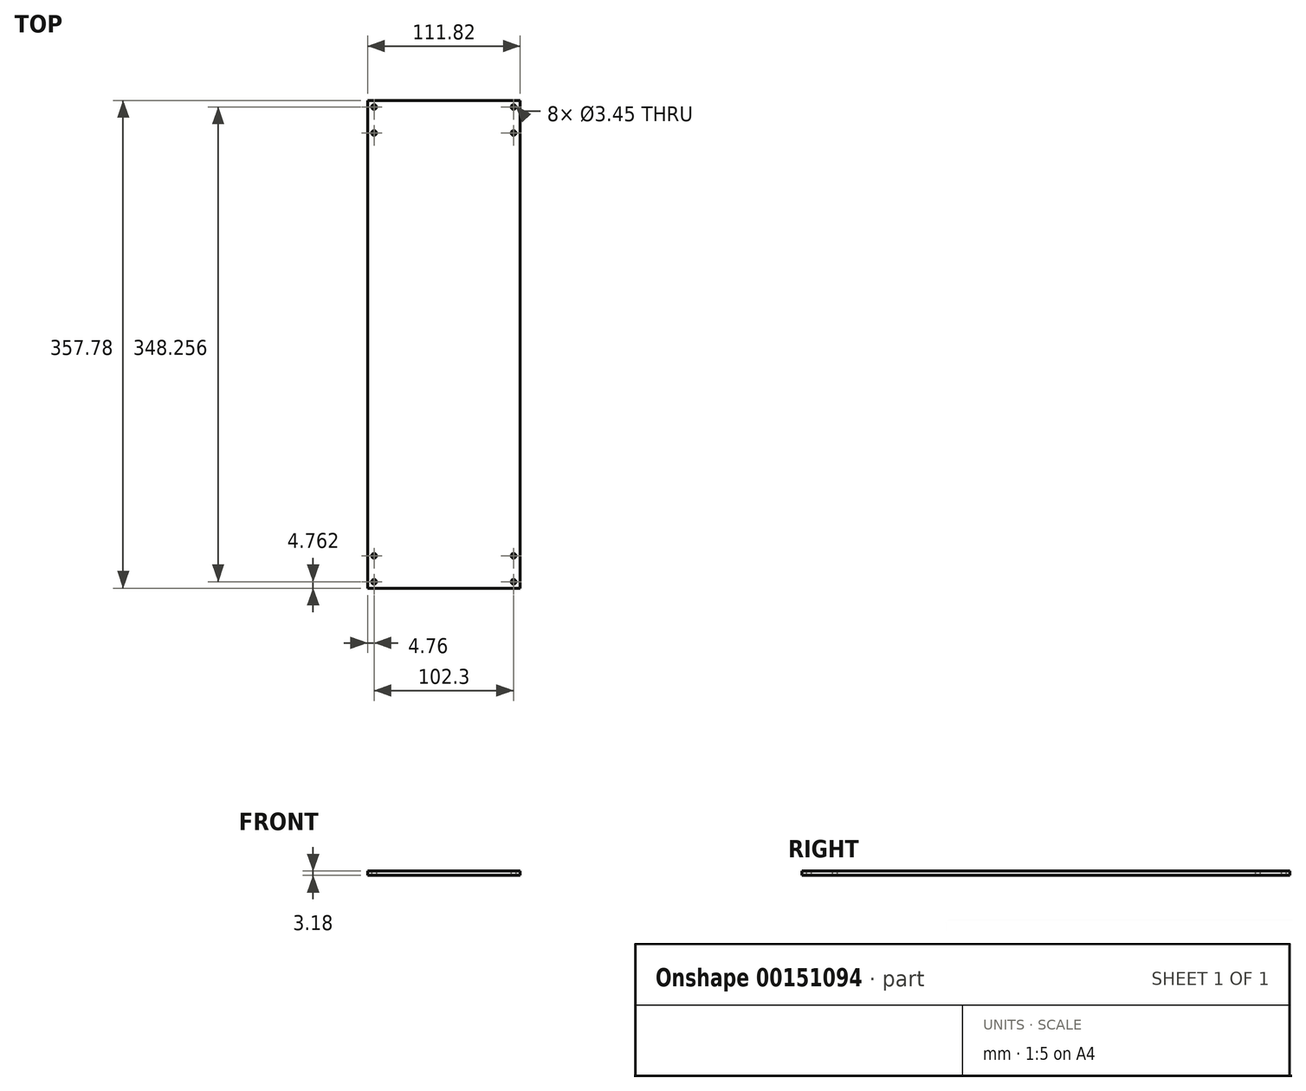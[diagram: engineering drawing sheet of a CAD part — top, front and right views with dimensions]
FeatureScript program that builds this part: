
annotation { "Feature Type Name" : "Feature", "Feature Type Description" : "" }
export const myFeature = defineFeature(function(context is Context, id is Id, definition is map)
    precondition{}
    {
        {
            var Q0;
            Q0=qCreatedBy(makeId("Top.planeOp"),FACE);
            var sketch = newSketch(context, id + "F0", { "sketchPlane" : qUnion([Q0])});
            skLineSegment(sketch, "E0.bottom", {"start": v(55.91, -178.9) * mm, "end": v(-55.91, -178.9) * mm});
            skLineSegment(sketch, "E0.top", {"start": v(55.91, 178.9) * mm, "end": v(-55.91, 178.9) * mm});
            skLineSegment(sketch, "E0.left", {"start": v(55.91, -178.9) * mm, "end": v(55.91, 178.9) * mm});
            skLineSegment(sketch, "E0.right", {"start": v(-55.91, -178.9) * mm, "end": v(-55.91, 178.9) * mm});
            skPoint(sketch, "E0.middle", {"position": v(0, 0) * mm});
            skLineSegment(sketch, "E1", {"start": v(51.15, 155.08) * mm, "end": v(55.91, 155.08) * mm, "construction": true});
            skLineSegment(sketch, "E2.bottom", {"start": v(51.15, 155.08) * mm, "end": v(-51.15, 155.08) * mm, "construction": true});
            skLineSegment(sketch, "E2.top", {"start": v(51.15, -155.08) * mm, "end": v(-51.15, -155.08) * mm, "construction": true});
            skLineSegment(sketch, "E2.left", {"start": v(51.15, 155.08) * mm, "end": v(51.15, -155.08) * mm, "construction": true});
            skLineSegment(sketch, "E2.right", {"start": v(-51.15, 155.08) * mm, "end": v(-51.15, -155.08) * mm, "construction": true});
            skCircle(sketch, "E3", {"center": v(51.15, 155.08) * mm, "radius": 1.73 * mm});
            skCircle(sketch, "E4", {"center": v(-51.15, -155.08) * mm, "radius": 1.73 * mm});
            skLineSegment(sketch, "E5", {"start": v(0, 155.08) * mm, "end": v(0, 178.9) * mm, "construction": true});
            skLineSegment(sketch, "E6", {"start": v(51.15, 155.08) * mm, "end": v(51.15, 174.13) * mm, "construction": true});
            skCircle(sketch, "E7", {"center": v(-51.15, 155.08) * mm, "radius": 1.73 * mm});
            skCircle(sketch, "E8", {"center": v(51.15, -155.08) * mm, "radius": 1.73 * mm});
            skLineSegment(sketch, "E9", {"start": v(51.15, 174.13) * mm, "end": v(51.15, 178.9) * mm, "construction": true});
            skCircle(sketch, "E10", {"center": v(51.15, 174.13) * mm, "radius": 1.73 * mm});
            skLineSegment(sketch, "E11", {"start": v(-51.15, 155.08) * mm, "end": v(-51.15, 174.13) * mm, "construction": true});
            skLineSegment(sketch, "E12", {"start": v(-51.15, 174.13) * mm, "end": v(-51.15, 178.9) * mm, "construction": true});
            skLineSegment(sketch, "E13", {"start": v(-51.15, -155.08) * mm, "end": v(-51.15, -174.13) * mm, "construction": true});
            skLineSegment(sketch, "E14", {"start": v(-51.15, -174.13) * mm, "end": v(-51.15, -178.9) * mm, "construction": true});
            skLineSegment(sketch, "E15", {"start": v(51.15, -155.08) * mm, "end": v(51.15, -174.13) * mm, "construction": true});
            skLineSegment(sketch, "E16", {"start": v(51.15, -174.13) * mm, "end": v(51.15, -178.9) * mm, "construction": true});
            skCircle(sketch, "E17", {"center": v(-51.15, 174.13) * mm, "radius": 1.73 * mm});
            skCircle(sketch, "E18", {"center": v(-51.15, -174.13) * mm, "radius": 1.73 * mm});
            skCircle(sketch, "E19", {"center": v(51.15, -174.13) * mm, "radius": 1.73 * mm});
            skSolve(sketch);
        }
        {
            var Q0;
            Q0=makeQuery(id+"F0.imprint","IMPRINT",FACE,{"disambiguationData":[TD([[makeQuery(id+"F0.imprint","IMPRINT",EDGE,{"derivedFrom":sQuery(id+"F0.wireOp",EDGE,"E0.bottom")}),-1.0]])]});
            extrude(context, id + "F1", {"entities" : qUnion([Q0]), "depth" : 3.17 * mm});
        }
    });
